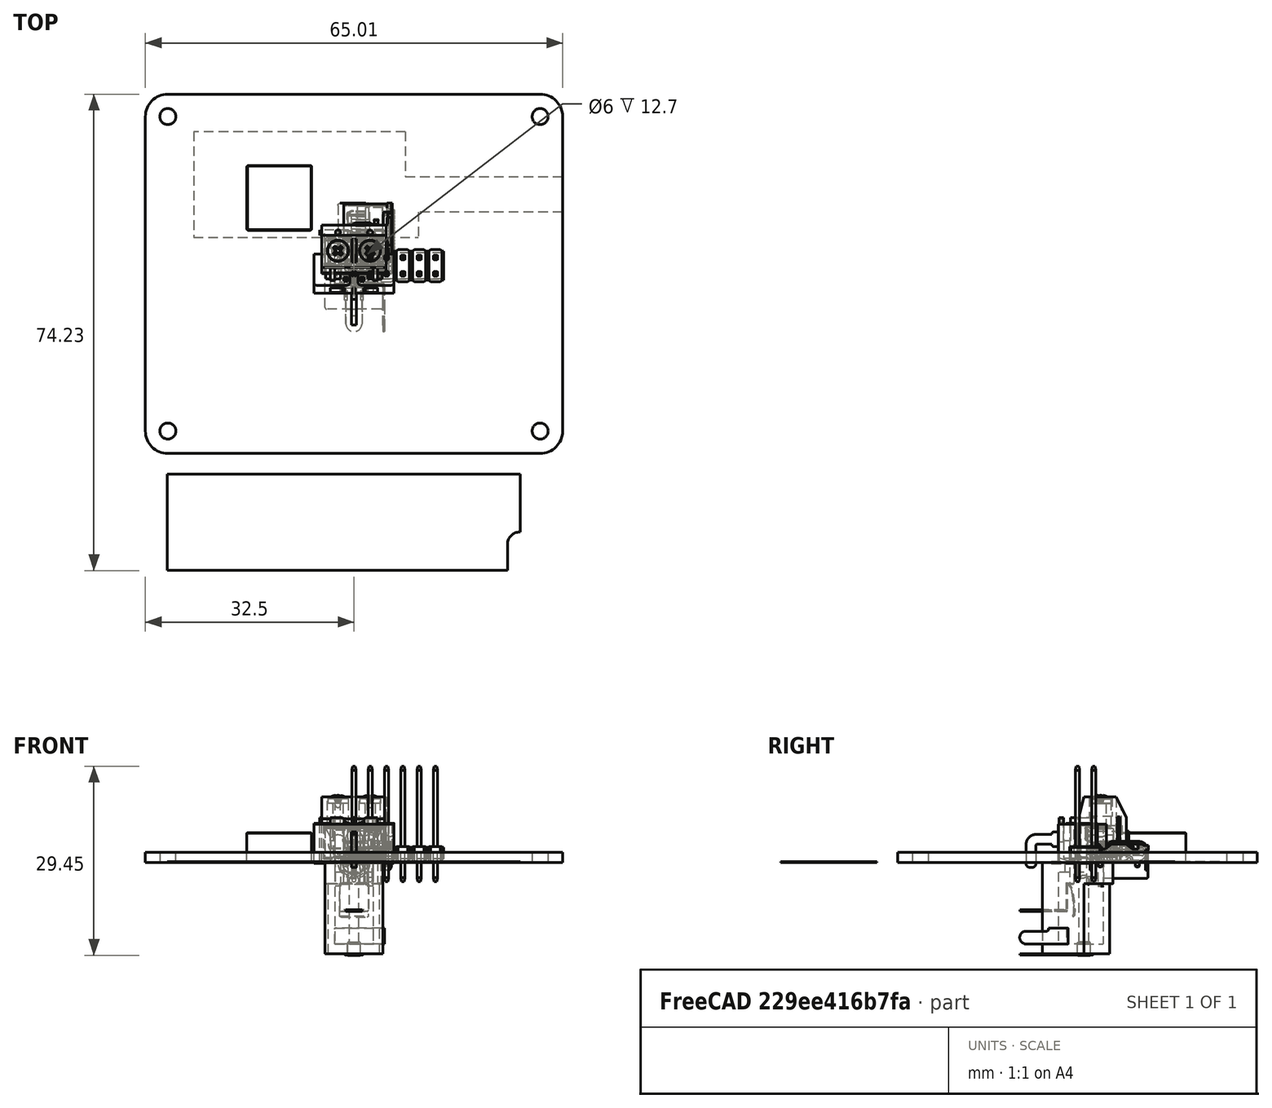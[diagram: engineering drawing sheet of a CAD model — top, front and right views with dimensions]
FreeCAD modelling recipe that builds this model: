
FCSTD DOCUMENT  (FreeCAD 1.0R39109 (Git))
Label: Yahboom PDB
License: All rights reserved
LicenseURL: https://en.wikipedia.org/wiki/All_rights_reserved
objects: Part::Feature×40, App::Link×16, App::FeaturePython×16, Sketcher::SketchObject×10, App::Part×9, PartDesign::Pad×7, PartDesign::Body×7, PartDesign::Fillet×5, App::DocumentObjectGroup×3, PartDesign::Pocket×2, PartDesign::Chamfer×2, Part::Extrusion×1, PartDesign::FeatureBase×1, Assembly::JointGroup×1, Assembly::AssemblyObject×1
note: 118 computed .brp shape members not serialized (recipe doc carries the construction recipe); baked Part::Feature solids carry a one-line shape summary decoded from their .brp

FEATURE [Sketcher::SketchObject] Sketch001
  ArcFitTolerance = 1e-06
  AttachmentSupport = -> [XY_Plane001]
  FullyConstrained = true
  MakeInternals = false
  MapMode = 5
  sketch-geometry (23):
    g0: LineSegment StartX=-32.5 StartY=24.5 StartZ=0 EndX=-32.5 EndY=-24.5 EndZ=0
    g1: LineSegment StartX=-29 StartY=-28 StartZ=0 EndX=29 EndY=-28 EndZ=0
    g2: LineSegment StartX=32.5 StartY=-24.5 StartZ=0 EndX=32.5 EndY=24.5 EndZ=0
    g3: LineSegment StartX=29 StartY=28 StartZ=0 EndX=-29 EndY=28 EndZ=0
    g4: Circle CenterX=-29 CenterY=-24.5 CenterZ=0 NormalX=0 NormalY=0 NormalZ=1 AngleXU=0 Radius=1.25
    g5: GeomPoint X=-32.5 Y=0 Z=0
    g6: GeomPoint X=0 Y=28 Z=0
    g7: Circle CenterX=29 CenterY=-24.5 CenterZ=0 NormalX=0 NormalY=0 NormalZ=1 AngleXU=0 Radius=1.25
    g8: LineSegment [constr] StartX=-29 StartY=-24.5 StartZ=0 EndX=29 EndY=-24.5 EndZ=0
    g9: LineSegment [constr] StartX=-29 StartY=-24.5 StartZ=0 EndX=-29 EndY=24.5 EndZ=0
    g10: LineSegment [constr] StartX=-29 StartY=24.5 StartZ=0 EndX=29 EndY=24.5 EndZ=0
    g11: Circle CenterX=-29 CenterY=24.5 CenterZ=0 NormalX=0 NormalY=0 NormalZ=1 AngleXU=0 Radius=1.25
    g12: Circle CenterX=29 CenterY=24.5 CenterZ=0 NormalX=0 NormalY=0 NormalZ=1 AngleXU=0 Radius=1.25
    g13: GeomPoint [constr] X=-29 Y=0 Z=0
    g14: ArcOfCircle CenterX=-29 CenterY=24.5 CenterZ=0 NormalX=0 NormalY=0 NormalZ=1 AngleXU=0 Radius=3.5 StartAngle=1.5708 EndAngle=3.14159
    g15: GeomPoint [constr] X=-32.5 Y=28 Z=0
    g16: ArcOfCircle CenterX=29 CenterY=24.5 CenterZ=0 NormalX=0 NormalY=0 NormalZ=1 AngleXU=0 Radius=3.5 StartAngle=0 EndAngle=1.5708
    g17: GeomPoint [constr] X=32.5 Y=28 Z=0
    g18: ArcOfCircle CenterX=-29 CenterY=-24.5 CenterZ=0 NormalX=0 NormalY=0 NormalZ=1 AngleXU=0 Radius=3.5 StartAngle=3.14159 EndAngle=4.71239
    g19: GeomPoint [constr] X=-32.5 Y=-28 Z=0
    g20: ArcOfCircle CenterX=29 CenterY=-24.5 CenterZ=0 NormalX=0 NormalY=0 NormalZ=1 AngleXU=0 Radius=3.5 StartAngle=4.71239 EndAngle=6.28319
    g21: GeomPoint [constr] X=32.5 Y=-28 Z=0
    g22: GeomPoint X=0 Y=24.5 Z=0
  constraints (50):
    c: Vertical(g0)
    c: Vertical(g2)
    c: Horizontal(g1)
    c: Horizontal(g3)
    c: DistanceX(g15,g17) = 65
    c: DistanceY(g19,g15) = 56
    c: Diameter(g4) = 2.5
    c: Symmetric(g15,g19,g5)
    c: Horizontal(g5,g-1)
    c: Symmetric(g17,g15,g6)
    c: Vertical(g6,g-1)
    c: Diameter(g7) = 2.5
    c: Horizontal(g4,g7)
    c: Coincident(g8,g4)
    c: Coincident(g8,g7)
    c: Vertical(g9)
    c: Coincident(g10,g9)
    c: Horizontal(g10)
    c: Coincident(g11,g9)
    c: Coincident(g12,g10)
    c: Diameter(g11) = 2.5
    c: Diameter(g12) = 2.5
    c: DistanceX(g8,g8) = 58
    c: DistanceY(g9,g9) = 49
    c: DistanceX(g10,g10) = 58
    c: Coincident(g9,g4)
    c: Symmetric(g9,g9,g13)
    c: Horizontal(g13,g-1)
    c: PointOnObject(g15,g0)
    c: PointOnObject(g15,g3)
    c: Tangent(g0,g14) = -1.5708
    c: Tangent(g3,g14) = -1.5708
    c: PointOnObject(g17,g2)
    c: PointOnObject(g17,g3)
    c: Tangent(g2,g16) = -1.5708
    c: Tangent(g3,g16) = -1.5708
    c: PointOnObject(g19,g0)
    c: PointOnObject(g19,g1)
    c: Tangent(g0,g18) = -1.5708
    c: Tangent(g1,g18) = -1.5708
    c: PointOnObject(g21,g1)
    c: PointOnObject(g21,g2)
    c: Tangent(g1,g20) = -1.5708
    c: Tangent(g2,g20) = -1.5708
    c: Radius(g14) = 3.5
    c: Radius(g16) = 3.5
    c: Radius(g20) = 3.5
    c: Radius(g18) = 3.5
    c: Symmetric(g10,g10,g22)
    c: Vertical(g22,g-1)
FEATURE [PartDesign::Pad] Pad
  Direction = (0,0,1)
  Length = 1.57
  Length2 = 10
  Profile = -> Sketch001
  ReferenceAxis = -> Sketch001 [N_Axis]
  Refine = true
  Suppressed = false
  Type = 0
FEATURE [PartDesign::Body] Body  label="Board"
  AllowCompound = false
  Group = -> [Sketch001,Pad]
  Origin = -> Origin001
  Tip = -> Pad
FEATURE [Part::Feature] Part__Feature001  label="XH 2,54_2p"
  shape: bbox 7.4 x 5.75 x 7 mm, 52 faces (baked)
FEATURE [Part::Feature] Part__Feature002  label="XH 2,54_2p001"
  shape: bbox 0.64 x 0.64 x 9.7 mm, 14 faces (baked)
FEATURE [Part::Feature] Part__Feature003  label="XH 2,54_2p002"
  shape: bbox 0.64 x 0.64 x 9.7 mm, 14 faces (baked)
FEATURE [App::Part] XH_2_54_2p  label="XH 2,54_2p003"
  Group = -> [Part__Feature001,Part__Feature002,Part__Feature003]
  Origin = -> Origin002
FEATURE [Part::Feature] Part__Feature005  label="DC_JACK v003"
  shape: bbox 3.248 x 11.62 x 12.45 mm, 13 faces (baked)
FEATURE [Part::Feature] Part__Feature006  label="DC_JACK v004"
  shape: bbox 4.51 x 8.656 x 5.34 mm, 18 faces (baked)
FEATURE [Part::Feature] Part__Feature007  label="DC_JACK v005"
  shape: bbox 7.75 x 7.5 x 2.5 mm, 13 faces (baked)
FEATURE [App::Link] DC_JACK_v006  label="DC_JACK v007"
  LinkPlacement = pos=(2.3,28,7.07) rot=(0,0.707107,0.707107;3.14159rad)
  LinkedObject = -> DC_JACK_v2
  Placement = pos=(2.3,28,7.07) rot=(0,0.707107,0.707107;3.14159rad)
FEATURE [App::Link] XH_2_54_2p003  label="XH 2,54_2p004"
  LinkPlacement = pos=(-8.13,21,4.445) rot=(1,0,0;4.71239rad)
  LinkedObject = -> XH_2_54_2p
  Placement = pos=(-8.13,21,4.445) rot=(1,0,0;4.71239rad)
FEATURE [Part::Feature] Part__Feature016  label="USB Type C"
  Placement = pos=(4.7601,6.43113,0.0823619) rot=(0.57735,0.57735,0.57735;2.0944rad)
  shape: bbox 7.401 x 8.941 x 4.471 mm, 192 faces (baked)
FEATURE [Part::Feature] Part__Feature017  label="USB Type C001"
  Placement = pos=(4.7601,6.43113,0.0823619) rot=(0.57735,0.57735,0.57735;2.0944rad)
  shape: bbox 0.5 x 0.3 x 1.1 mm, 6 faces (baked)
FEATURE [Part::Feature] Part__Feature018  label="USB Type C002"
  Placement = pos=(4.7601,6.43113,0.0823619) rot=(0.57735,0.57735,0.57735;2.0944rad)
  shape: bbox 7.5 x 9.2 x 3.55 mm, 355 faces (baked)
FEATURE [Part::Feature] Part__Feature019  label="USB Type C003"
  Placement = pos=(4.7601,6.43113,0.0823619) rot=(0.57735,0.57735,0.57735;2.0944rad)
  shape: bbox 0.5 x 0.3 x 1.1 mm, 6 faces (baked)
FEATURE [App::Part] USB_Type_C  label="USB Type C004"
  Group = -> [Part__Feature016,Part__Feature017,Part__Feature018,Part__Feature019]
  Origin = -> Origin007
FEATURE [Part::Feature] Part__Feature020  label="B2B-PH-K-S v3"
  shape: bbox 5.9 x 4.5 x 6 mm, 52 faces (baked)
FEATURE [Part::Feature] Part__Feature021  label="B2B-PH-K-S v004"
  shape: bbox 0.5 x 0.5 x 8.4 mm, 14 faces (baked)
FEATURE [Part::Feature] Part__Feature022  label="B2B-PH-K-S v005"
  shape: bbox 0.5 x 0.5 x 8.4 mm, 14 faces (baked)
FEATURE [App::Part] B2B_PH_K_S_v3  label="B2B-PH-K-S v006"
  Group = -> [Part__Feature020,Part__Feature021,Part__Feature022]
  Origin = -> Origin008
FEATURE [App::Link] DC_JACK_v007  label="DC_JACK v008"
  LinkPlacement = pos=(2.3,-28,7.07) rot=(1,0,0;1.5708rad)
  LinkedObject = -> DC_JACK_v2
  Placement = pos=(2.3,-28,7.07) rot=(1,0,0;1.5708rad)
FEATURE [App::Link] USB_Type_C004  label="USB Type C005"
  LinkPlacement = pos=(-15.0042,-27.4101,1.52835) rot=(0,0,1;1.5708rad)
  LinkedObject = -> USB_Type_C
  Placement = pos=(-15.0042,-27.4101,1.52835) rot=(0,0,1;1.5708rad)
FEATURE [App::Link] B2B_PH_K_S_v006  label="B2B-PH-K-S v007"
  LinkPlacement = pos=(-10,-22,6.07) rot=(0,0.707107,-0.707107;3.14159rad)
  LinkedObject = -> B2B_PH_K_S_v3
  Placement = pos=(-10,-22,6.07) rot=(0,0.707107,-0.707107;3.14159rad)
FEATURE [App::Link] B2B_PH_K_S_v007  label="B2B-PH-K-S v008"
  LinkPlacement = pos=(-3.6,-22,6.07) rot=(0,0.707107,-0.707107;3.14159rad)
  LinkedObject = -> B2B_PH_K_S_v3
  Placement = pos=(-3.6,-22,6.07) rot=(0,0.707107,-0.707107;3.14159rad)
FEATURE [Part::Feature] Part__Feature023  label="case"
  shape: bbox 10.35 x 7.6 x 10.2 mm, 52 faces (baked)
FEATURE [Part::Feature] Part__Feature024  label="Terminal1"
  Placement = pos=(2.5,5.6,0) rot=(0,0,1;0rad)
  shape: bbox 4 x 4.06 x 3.567 mm, 29 faces (baked)
FEATURE [Part::Feature] Part__Feature025  label="Terminal002"
  Placement = pos=(2.5,5.6,0) rot=(0,0,1;0rad)
  shape: bbox 4 x 4 x 9 mm, 10 faces (baked)
FEATURE [App::Part] Terminal1  label="Terminal003"
  Group = -> [Part__Feature024,Part__Feature025]
  Origin = -> Origin010
FEATURE [Part::Feature] Part__Feature026  label="Terminal004"
  Placement = pos=(-2.5,5.6,0) rot=(0,0,1;0rad)
  shape: bbox 4 x 4.06 x 3.567 mm, 29 faces (baked)
FEATURE [Part::Feature] Part__Feature027  label="Terminal005"
  Placement = pos=(-2.5,5.6,0) rot=(0,0,1;0rad)
  shape: bbox 4 x 4 x 9 mm, 10 faces (baked)
FEATURE [App::Part] Terminal002  label="Terminal006"
  Group = -> [Part__Feature026,Part__Feature027]
  Origin = -> Origin011
FEATURE [Part::Feature] Part__Feature028  label="Screw1"
  Placement = pos=(-2.5,3.6,9.2) rot=(0,0,1;0rad)
  shape: bbox 3.2 x 3.2 x 5.262 mm, 27 faces (baked)
FEATURE [Part::Feature] Part__Feature029  label="Screw002"
  Placement = pos=(2.5,3.6,9.2) rot=(0,0,1;0rad)
  shape: bbox 3.2 x 3.2 x 5.262 mm, 27 faces (baked)
FEATURE [App::Part] kf301_v1
  Group = -> [Part__Feature023,Terminal1,Terminal002,Part__Feature028,Part__Feature029]
  Origin = -> Origin009
FEATURE [App::Link] kf301_v002
  LinkPlacement = pos=(-19.5,27.6021,1.57) rot=(0,0,1;3.14159rad)
  LinkedObject = -> kf301_v1
  Placement = pos=(-19.5,27.6021,1.57) rot=(0,0,1;3.14159rad)
FEATURE [App::FeaturePython] Joint  label="Fixed"  # Assembly joint (typed FeaturePython)
  Activated = true
  AngleMax = 0
  AngleMin = 0
  Detach1 = false
  Detach2 = false
  Distance = 0
  Distance2 = 0
  EnableAngleMax = false
  EnableAngleMin = false
  EnableLengthMax = false
  EnableLengthMin = false
  JointType = 0 (Fixed)
  LengthMax = 0
  LengthMin = 0
  Offset1 = pos=(0,8,0) rot=(0,0,1;0rad)
  Placement1 = pos=(13,3.10207,2e-15) rot=(-0.57735,-0.57735,0.57735;4.18879rad)
  Placement2 = pos=(-32.5,24.5,1.57) rot=(-0.57735,-0.57735,0.57735;4.18879rad)
  Reference1 = -> Assembly [kf301_v002.Part__Feature023.Edge33,kf301_v002.Part__Feature023.Edge33]
  Reference2 = -> Assembly [Board.Edge4,Board.Vertex2]
FEATURE [App::FeaturePython] Joint001  label="Fixed001"  # Assembly joint (typed FeaturePython)
  Activated = true
  AngleMax = 0
  AngleMin = 0
  Detach1 = false
  Detach2 = false
  Distance = 0
  Distance2 = 0
  EnableAngleMax = false
  EnableAngleMin = false
  EnableLengthMax = false
  EnableLengthMin = false
  JointType = 0 (Fixed)
  LengthMax = 0
  LengthMin = 0
  Offset2 = pos=(0,20.67,-3.5) rot=(0,0,-1;1.5708rad)
  Placement1 = pos=(-3.7,2.875,7) rot=(0,1,0;3.14159rad)
  Placement2 = pos=(-11.83,28,1.57) rot=(0,-0.707107,0.707107;3.14159rad)
  Reference1 = -> Assembly [XH_2_54_2p003.Part__Feature001.Edge107,XH_2_54_2p003.Part__Feature001.Vertex73]
  Reference2 = -> Assembly [Board.Edge4,Board.Vertex2]
FEATURE [App::FeaturePython] Joint003  label="Fixed003"  # Assembly joint (typed FeaturePython)
  Activated = true
  AngleMax = 0
  AngleMin = 0
  Detach1 = false
  Detach2 = false
  Distance = 0
  Distance2 = 0
  EnableAngleMax = false
  EnableAngleMin = false
  EnableLengthMax = false
  EnableLengthMin = false
  JointType = 0 (Fixed)
  LengthMax = 0
  LengthMin = 0
  Offset2 = pos=(0,30.55,-3.6) rot=(0,0,-1;1.5708rad)
  Placement1 = pos=(-4.25,-5.5,-7.1) rot=(0,1,0;3.14159rad)
  Placement2 = pos=(-1.95,-20.9,1.57) rot=(0,-0.707107,0.707107;3.14159rad)
  Reference1 = -> Assembly [DC_JACK_v007.Part__Feature004.Edge68,DC_JACK_v007.Part__Feature004.Edge68]
  Reference2 = -> Assembly [Board.Edge4,Board.Vertex4]
FEATURE [Part::Feature] Part__Feature004  label="DC_JACK v2"
  shape: bbox 9 x 11 x 14.2 mm, 28 faces (baked)
FEATURE [App::Part] DC_JACK_v2  label="DC_JACK v006"
  Group = -> [Part__Feature004,Part__Feature005,Part__Feature006,Part__Feature007]
  Origin = -> Origin003
FEATURE [App::Link] Board  label="Board001"
  LinkedObject = -> Body
FEATURE [App::FeaturePython] GroundedJoint  # Assembly grounded joint (typed FeaturePython)
  ObjectToGround = -> Board
FEATURE [App::FeaturePython] Joint004  label="Fixed004"  # Assembly joint (typed FeaturePython)
  Activated = true
  AngleMax = 0
  AngleMin = 0
  Detach1 = false
  Detach2 = false
  Distance = 0
  Distance2 = 0
  EnableAngleMax = false
  EnableAngleMin = false
  EnableLengthMax = false
  EnableLengthMin = false
  JointType = 0 (Fixed)
  LengthMax = 0
  LengthMin = 0
  Offset2 = pos=(0,30.55,-3.5) rot=(0,0,1;1.5708rad)
  Placement1 = pos=(4.25,-5.5,0) rot=(0,1,0;3.14159rad)
  Placement2 = pos=(-1.95,28,1.57) rot=(-1,0,0;4.71239rad)
  Reference1 = -> Assembly [DC_JACK_v006.Part__Feature004.Edge70,DC_JACK_v006.Part__Feature004.Vertex46]
  Reference2 = -> Assembly [Board.Edge4,Board.Vertex2]
FEATURE [App::FeaturePython] Joint005  label="Fixed005"  # Assembly joint (typed FeaturePython)
  Activated = true
  AngleMax = 0
  AngleMin = 0
  Detach1 = false
  Detach2 = false
  Distance = 0
  Distance2 = 0
  EnableAngleMax = false
  EnableAngleMin = false
  EnableLengthMax = false
  EnableLengthMin = false
  JointType = 0 (Fixed)
  LengthMax = 0
  LengthMin = 0
  Offset2 = pos=(0,1,5.85) rot=(0,0,-1;1.5708rad)
  Placement1 = pos=(1.71465,-0.0407081,-6.35) rot=(0.707107,0,0.707107;3.14159rad)
  Placement2 = pos=(-23.15,-29,1.57) rot=(0.57735,0.57735,0.57735;2.0944rad)
  Reference1 = -> Assembly [USB_Type_C004.Part__Feature016.Edge38,USB_Type_C004.Part__Feature016.Edge38]
  Reference2 = -> Assembly [Board.Edge10,Board.Vertex6]
FEATURE [App::FeaturePython] Joint006  label="Fixed006"  # Assembly joint (typed FeaturePython)
  Activated = true
  AngleMax = 0
  AngleMin = 0
  Detach1 = false
  Detach2 = false
  Distance = 0
  Distance2 = 0
  EnableAngleMax = false
  EnableAngleMin = false
  EnableLengthMax = false
  EnableLengthMin = false
  JointType = 0 (Fixed)
  LengthMax = 0
  LengthMin = 0
  Offset2 = pos=(0,16.6,0.5) rot=(0,0,1;1.5708rad)
  Placement1 = pos=(5.9,4.5,3) rot=(0,1,0;3.14159rad)
  Placement2 = pos=(-15.9,-25,1.57) rot=(-1,0,0;4.71239rad)
  Reference1 = -> Assembly [B2B_PH_K_S_v006.Part__Feature020.Edge155,B2B_PH_K_S_v006.Part__Feature020.Edge155]
  Reference2 = -> Assembly [Board.Edge4,Board.Vertex4]
FEATURE [App::FeaturePython] Joint007  label="Fixed007"  # Assembly joint (typed FeaturePython)
  Activated = true
  AngleMax = 0
  AngleMin = 0
  Detach1 = false
  Detach2 = false
  Distance = 0
  Distance2 = 0
  EnableAngleMax = false
  EnableAngleMin = false
  EnableLengthMax = false
  EnableLengthMin = false
  JointType = 0 (Fixed)
  LengthMax = 0
  LengthMin = 0
  Offset2 = pos=(0,23,0.5) rot=(0,0,1;1.5708rad)
  Placement1 = pos=(5.9,4.5,3) rot=(0,1,0;3.14159rad)
  Placement2 = pos=(-9.5,-25,1.57) rot=(-1,0,0;4.71239rad)
  Reference1 = -> Assembly [B2B_PH_K_S_v007.Part__Feature020.Edge155,B2B_PH_K_S_v007.Part__Feature020.Edge155]
  Reference2 = -> Assembly [Board.Edge4,Board.Vertex4]
FEATURE [Part::Feature] Part__Feature  label="4.7uF 63V electr 5 x11mm -P.diameter 2.5mm-Green-Yellow"
  shape: bbox 5.721 x 15.1 x 5.727 mm, 151 faces (baked)
FEATURE [App::Link] __7uF_63V_electr_5_x11mm__P_diameter_2_5mm_Green_Yellow  label="4.7uF 63V electr 5 x11mm -P.diameter 2.5mm-Green-Yellow001"
  LinkPlacement = pos=(29.0455,3.315,4.13) rot=(0,0,1;0rad)
  LinkedObject = -> Part__Feature
  Placement = pos=(29.0455,3.315,4.13) rot=(0,0,1;0rad)
FEATURE [App::Link] __7uF_63V_electr_5_x11mm__P_diameter_2_5mm_Green_Yellow001  label="4.7uF 63V electr 5 x11mm -P.diameter 2.5mm-Green-Yellow002"
  LinkPlacement = pos=(-29.0458,3.3,4.145) rot=(0,0,1;0rad)
  LinkedObject = -> Part__Feature
  Placement = pos=(-29.0458,3.3,4.145) rot=(0,0,1;0rad)
FEATURE [App::Link] __7uF_63V_electr_5_x11mm__P_diameter_2_5mm_Green_Yellow002  label="4.7uF 63V electr 5 x11mm -P.diameter 2.5mm-Green-Yellow003"
  LinkPlacement = pos=(-29.0458,-3.65,4.145) rot=(0,0,1;3.14159rad)
  LinkedObject = -> Part__Feature
  Placement = pos=(-29.0458,-3.65,4.145) rot=(0,0,1;3.14159rad)
FEATURE [App::FeaturePython] Joint008  label="Fixed008"  # Assembly joint (typed FeaturePython)
  Activated = true
  AngleMax = 0
  AngleMin = 0
  Detach1 = false
  Detach2 = false
  Distance = 0
  Distance2 = 0
  EnableAngleMax = false
  EnableAngleMin = false
  EnableLengthMax = false
  EnableLengthMin = false
  JointType = 0 (Fixed)
  LengthMax = 0
  LengthMin = 0
  Offset2 = pos=(-2.5,13.75,-1) rot=(0,0,1;3.14159rad)
  Placement1 = pos=(0.9545,10.935,-0.06) rot=(0.707107,0,0.707107;3.14159rad)
  Placement2 = pos=(30,14.25,4.07) rot=(0,1,0;4.71239rad)
  Reference1 = -> Assembly [__7uF_63V_electr_5_x11mm__P_diameter_2_5mm_Green_Yellow.Edge464,__7uF_63V_electr_5_x11mm__P_diameter_2_5mm_Green_Yellow.Edge464]
  Reference2 = -> Assembly [Board.Edge22,Board.Vertex14]
FEATURE [App::FeaturePython] Joint009  label="Fixed009"  # Assembly joint (typed FeaturePython)
  Activated = true
  AngleMax = 0
  AngleMin = 0
  Detach1 = false
  Detach2 = false
  Distance = 0
  Distance2 = 0
  EnableAngleMax = false
  EnableAngleMin = false
  EnableLengthMax = false
  EnableLengthMin = false
  JointType = 0 (Fixed)
  LengthMax = 0
  LengthMin = 0
  Offset2 = pos=(-2.5,13.75,1) rot=(0,0,1;0rad)
  Placement1 = pos=(-0.954218,10.95,-0.075) rot=(-0.707107,0,0.707107;3.14159rad)
  Placement2 = pos=(-30,14.25,4.07) rot=(-0.707107,0,0.707107;3.14159rad)
  Reference1 = -> Assembly [__7uF_63V_electr_5_x11mm__P_diameter_2_5mm_Green_Yellow001.Edge490,__7uF_63V_electr_5_x11mm__P_diameter_2_5mm_Green_Yellow001.Edge490]
  Reference2 = -> Assembly [Board.Edge22,Board.Vertex16]
FEATURE [App::FeaturePython] Joint010  label="Fixed010"  # Assembly joint (typed FeaturePython)
  Activated = true
  AngleMax = 0
  AngleMin = 0
  Detach1 = false
  Detach2 = false
  Distance = 0
  Distance2 = 0
  EnableAngleMax = false
  EnableAngleMin = false
  EnableLengthMax = false
  EnableLengthMin = false
  JointType = 0 (Fixed)
  LengthMax = 0
  LengthMin = 0
  Offset2 = pos=(2.5,-13.4,-1) rot=(0,0,1;3.14159rad)
  Placement1 = pos=(0.954218,10.95,-0.075) rot=(-0.707107,0,0.707107;3.14159rad)
  Placement2 = pos=(-30,-14.6,4.07) rot=(0,-1,0;4.71239rad)
  Reference1 = -> Assembly [__7uF_63V_electr_5_x11mm__P_diameter_2_5mm_Green_Yellow002.Edge463,__7uF_63V_electr_5_x11mm__P_diameter_2_5mm_Green_Yellow002.Edge463]
  Reference2 = -> Assembly [Board.Edge10,Board.Vertex6]
FEATURE [Part::Feature] Part__Feature030  label="DS1021_black_2x06p_100mil_Type5_rev1.0"
  shape: bbox 0.64 x 0.64 x 18 mm, 18 faces (baked)
FEATURE [Part::Feature] Part__Feature031  label="DS1021_black_2x06p_100mil_Type5_rev1.001"
  shape: bbox 2.54 x 5 x 2.5 mm, 30 faces (baked)
FEATURE [Part::Feature] Part__Feature032  label="DS1021_black_2x06p_100mil_Type5_rev1.002"
  shape: bbox 2.54 x 5 x 2.5 mm, 30 faces (baked)
FEATURE [Part::Feature] Part__Feature033  label="DS1021_black_2x06p_100mil_Type5_rev1.003"
  shape: bbox 0.64 x 0.64 x 18 mm, 18 faces (baked)
FEATURE [Part::Feature] Part__Feature034  label="DS1021_black_2x06p_100mil_Type5_rev1.004"
  shape: bbox 0.64 x 0.64 x 18 mm, 18 faces (baked)
FEATURE [Part::Feature] Part__Feature035  label="DS1021_black_2x06p_100mil_Type5_rev1.005"
  shape: bbox 0.64 x 0.64 x 18 mm, 18 faces (baked)
FEATURE [Part::Feature] Part__Feature036  label="DS1021_black_2x06p_100mil_Type5_rev1.006"
  shape: bbox 0.64 x 0.64 x 18 mm, 18 faces (baked)
FEATURE [Part::Feature] Part__Feature037  label="DS1021_black_2x06p_100mil_Type5_rev1.007"
  shape: bbox 0.64 x 0.64 x 18 mm, 18 faces (baked)
FEATURE [Part::Feature] Part__Feature008  label="DS1021_black_2x06p_100mil_Type5_rev1.008"
  shape: bbox 2.54 x 5 x 2.5 mm, 30 faces (baked)
FEATURE [Part::Feature] Part__Feature009  label="DS1021_black_2x06p_100mil_Type5_rev1.009"
  shape: bbox 0.64 x 0.64 x 18 mm, 18 faces (baked)
FEATURE [Part::Feature] Part__Feature010  label="DS1021_black_2x06p_100mil_Type5_rev1.010"
  shape: bbox 0.64 x 0.64 x 18 mm, 18 faces (baked)
FEATURE [Part::Feature] Part__Feature011  label="DS1021_black_2x06p_100mil_Type5_rev1.011"
  shape: bbox 2.54 x 5 x 2.5 mm, 30 faces (baked)
FEATURE [Part::Feature] Part__Feature012  label="DS1021_black_2x06p_100mil_Type5_rev1.012"
  shape: bbox 2.54 x 5 x 2.5 mm, 30 faces (baked)
FEATURE [Part::Feature] Part__Feature013  label="DS1021_black_2x06p_100mil_Type5_rev1.013"
  shape: bbox 0.64 x 0.64 x 18 mm, 18 faces (baked)
FEATURE [Part::Feature] Part__Feature014  label="DS1021_black_2x06p_100mil_Type5_rev1.014"
  shape: bbox 0.64 x 0.64 x 18 mm, 18 faces (baked)
FEATURE [Part::Feature] Part__Feature015  label="DS1021_black_2x06p_100mil_Type5_rev1.015"
  shape: bbox 0.64 x 0.64 x 18 mm, 18 faces (baked)
FEATURE [Part::Feature] Part__Feature038  label="DS1021_black_2x06p_100mil_Type5_rev1.016"
  shape: bbox 0.64 x 0.64 x 18 mm, 18 faces (baked)
FEATURE [Part::Feature] Part__Feature039  label="DS1021_black_2x06p_100mil_Type5_rev1.017"
  shape: bbox 2.54 x 5 x 2.5 mm, 60 faces (baked)
FEATURE [App::Part] DS1021_black_2x06p_100mil_Type5_rev1_0  label="DS1021_black_2x06p_100mil_Type5_rev1.018"
  Group = -> [Part__Feature030,Part__Feature031,Part__Feature032,Part__Feature033,Part__Feature034,Part__Feature035,Part__Feature036,Part__Feature037,Part__Feature008,Part__Feature009,Part__Feature010,Part__Feature011,Part__Feature012,Part__Feature013,Part__Feature014,Part__Feature015,Part__Feature038,Part__Feature039]
  Origin = -> Origin012
FEATURE [App::Link] DS1021_black_2x06p_100mil_Type5_rev1_018  label="DS1021_black_2x06p_100mil_Type5_rev1.019"
  LinkPlacement = pos=(10.43,-13.025,2.77) rot=(1,0,0;1.5708rad)
  LinkedObject = -> DS1021_black_2x06p_100mil_Type5_rev1_0
  Placement = pos=(10.43,-13.025,2.77) rot=(1,0,0;1.5708rad)
FEATURE [App::FeaturePython] Joint011  label="Fixed011"  # Assembly joint (typed FeaturePython)
  Activated = true
  AngleMax = 0
  AngleMin = 0
  Detach1 = false
  Detach2 = false
  Distance = 0
  Distance2 = 0
  EnableAngleMax = false
  EnableAngleMin = false
  EnableLengthMax = false
  EnableLengthMin = false
  JointType = 0 (Fixed)
  LengthMax = 0
  LengthMin = 0
  Offset2 = pos=(0.2,-8.1,10) rot=(0,0,-1;1.5708rad)
  Placement1 = pos=(13.97,-1,1.475) rot=(0,1,0;3.14159rad)
  Placement2 = pos=(24.4,-14.5,1.77) rot=(0,0.707107,0.707107;3.14159rad)
  Reference1 = -> Assembly [DS1021_black_2x06p_100mil_Type5_rev1_018.Part__Feature012.Edge33,DS1021_black_2x06p_100mil_Type5_rev1_018.Part__Feature012.Edge33]
  Reference2 = -> Assembly [Board.Edge16,Board.Vertex10]
FEATURE [Sketcher::SketchObject] Sketch
  ArcFitTolerance = 1e-06
  FullyConstrained = true
  MakeInternals = false
  MapMode = 5
  sketch-geometry (6):
    g0: LineSegment StartX=6.25 StartY=-3 StartZ=0 EndX=6.25 EndY=3 EndZ=0
    g1: LineSegment StartX=6.25 StartY=3 StartZ=0 EndX=-6.25 EndY=3 EndZ=0
    g2: LineSegment StartX=-6.25 StartY=3 StartZ=0 EndX=-6.25 EndY=-3 EndZ=0
    g3: LineSegment StartX=-6.25 StartY=-3 StartZ=0 EndX=6.25 EndY=-3 EndZ=0
    g4: GeomPoint X=-6.25 Y=0 Z=0
    g5: GeomPoint X=0 Y=3 Z=0
  constraints (14):
    c: Coincident(g0,g1)
    c: Coincident(g1,g2)
    c: Coincident(g2,g3)
    c: Coincident(g3,g0)
    c: Vertical(g0)
    c: Vertical(g2)
    c: Horizontal(g1)
    c: Horizontal(g3)
    c: DistanceX(g1,g1) = 12.5
    c: DistanceY(g2,g2) = 6
    c: Symmetric(g2,g2,g4)
    c: Symmetric(g1,g1,g5)
    c: Vertical(g5,g-1)
    c: Horizontal(g4,g-1)
FEATURE [PartDesign::Pad] Pad001
  Direction = (0,0,1)
  Length = 6
  Length2 = 10
  Profile = -> Sketch
  ReferenceAxis = -> Sketch [N_Axis]
  Refine = true
  Suppressed = false
  Type = 0
FEATURE [Sketcher::SketchObject] Sketch002
  ArcFitTolerance = 1e-06
  AttachmentSupport = -> [YZ_Plane014]
  ExternalGeometry = -> [Pad001]
  FullyConstrained = true
  MakeInternals = false
  MapMode = 5
  Placement = pos=(0,0,0) rot=(0.57735,0.57735,0.57735;2.0944rad)
  sketch-geometry (12):
    g0: LineSegment StartX=-1.8 StartY=6 StartZ=0 EndX=3.1 EndY=6 EndZ=0
    g1: LineSegment StartX=3.1 StartY=6 StartZ=0 EndX=3.1 EndY=6.1 EndZ=0
    g2: LineSegment StartX=3.1 StartY=6.1 StartZ=0 EndX=-1.8 EndY=6.1 EndZ=0
    g3: LineSegment StartX=-1.8 StartY=6.1 StartZ=0 EndX=-1.8 EndY=6 EndZ=0
    g4: LineSegment StartX=3.1 StartY=6 StartZ=0 EndX=3 EndY=6 EndZ=0
    g5: LineSegment StartX=3 StartY=6 StartZ=0 EndX=3 EndY=-0.1 EndZ=0
    g6: LineSegment StartX=3 StartY=-0.1 StartZ=0 EndX=3.1 EndY=-0.1 EndZ=0
    g7: LineSegment StartX=3.1 StartY=-0.1 StartZ=0 EndX=3.1 EndY=6 EndZ=0
    g8: LineSegment StartX=3 StartY=-0.1 StartZ=0 EndX=3 EndY=-1e-16 EndZ=0
    g9: LineSegment StartX=3 StartY=-1e-16 StartZ=0 EndX=-1.8 EndY=-1e-16 EndZ=0
    g10: LineSegment StartX=-1.8 StartY=-1e-16 StartZ=0 EndX=-1.8 EndY=-0.1 EndZ=0
    g11: LineSegment StartX=-1.8 StartY=-0.1 StartZ=0 EndX=3 EndY=-0.1 EndZ=0
  constraints (34):
    c: Coincident(g0,g1)
    c: Coincident(g1,g2)
    c: Coincident(g2,g3)
    c: Coincident(g3,g0)
    c: Horizontal(g0)
    c: Horizontal(g2)
    c: Vertical(g1)
    c: Vertical(g3)
    c: Coincident(g4,g5)
    c: Coincident(g5,g6)
    c: Coincident(g6,g7)
    c: Coincident(g7,g4)
    c: Horizontal(g4)
    c: Horizontal(g6)
    c: Vertical(g5)
    c: Vertical(g7)
    c: Coincident(g4,g0)
    c: Coincident(g8,g9)
    c: Coincident(g9,g10)
    c: Coincident(g10,g11)
    c: Coincident(g11,g8)
    c: Vertical(g8)
    c: Vertical(g10)
    c: Horizontal(g9)
    c: Horizontal(g11)
    c: Coincident(g8,g5)
    c: Distance(g11,g9) = 0.1
    c: Distance(g7,g5) = 0.1
    c: Distance(g0,g2) = 0.1
    c: Distance(g-3,g3) = 1.2
    c: Vertical(g0,g9)
    c: Distance(g9,g0) = 6
    c: Distance(g-1,g0) = 6
    c: Distance(g-1,g5) = 3
FEATURE [Part::Extrusion] Extrude
  Base = -> Sketch002
  Dir = (1,0,0)
  DirMode = 2
  FaceMakerClass = Part::FaceMakerBullseye
  FaceMakerMode = 3
  LengthFwd = 12.5
  LengthRev = 0
  Solid = true
  Symmetric = true
FEATURE [Sketcher::SketchObject] Sketch003
  ArcFitTolerance = 1e-06
  AttachmentSupport = -> [Extrude]
  ExternalGeometry = -> [Extrude]
  FullyConstrained = true
  MakeInternals = false
  MapMode = 5
  Placement = pos=(0,0,6.1) rot=(0,0,1;0rad)
  sketch-geometry (14):
    g0: LineSegment StartX=-0.625 StartY=-1.8 StartZ=0 EndX=0.625 EndY=-1.8 EndZ=0
    g1: LineSegment StartX=0.625 StartY=-1.8 StartZ=0 EndX=0.625 EndY=0.7 EndZ=0
    g2: LineSegment StartX=0.625 StartY=0.7 StartZ=0 EndX=-0.625 EndY=0.7 EndZ=0
    g3: LineSegment StartX=-0.625 StartY=0.7 StartZ=0 EndX=-0.625 EndY=-1.8 EndZ=0
    g4: GeomPoint X=-2e-16 Y=-1.8 Z=0
    g5: GeomPoint X=-2e-16 Y=-1.8 Z=0
    g6: LineSegment StartX=2.125 StartY=0.7 StartZ=0 EndX=2.125 EndY=-0.8 EndZ=0
    g7: LineSegment StartX=2.125 StartY=-0.8 StartZ=0 EndX=4.375 EndY=-0.8 EndZ=0
    g8: LineSegment StartX=4.375 StartY=-0.8 StartZ=0 EndX=4.375 EndY=0.7 EndZ=0
    g9: LineSegment StartX=4.375 StartY=0.7 StartZ=0 EndX=2.125 EndY=0.7 EndZ=0
    g10: LineSegment StartX=-2.125 StartY=0.7 StartZ=0 EndX=-4.375 EndY=0.7 EndZ=0
    g11: LineSegment StartX=-4.375 StartY=0.7 StartZ=0 EndX=-4.375 EndY=-0.8 EndZ=0
    g12: LineSegment StartX=-4.375 StartY=-0.8 StartZ=0 EndX=-2.125 EndY=-0.8 EndZ=0
    g13: LineSegment StartX=-2.125 StartY=-0.8 StartZ=0 EndX=-2.125 EndY=0.7 EndZ=0
  constraints (38):
    c: Coincident(g0,g1)
    c: Coincident(g1,g2)
    c: Coincident(g2,g3)
    c: Coincident(g3,g0)
    c: Horizontal(g0)
    c: Horizontal(g2)
    c: Vertical(g1)
    c: Vertical(g3)
    c: Symmetric(g-3,g-3,g4)
    c: Symmetric(g0,g0,g5)
    c: Vertical(g4,g5)
    c: DistanceX(g2,g2) = 1.25
    c: DistanceY(g1,g1) = 2.5
    c: Coincident(g6,g7)
    c: Coincident(g7,g8)
    c: Coincident(g8,g9)
    c: Coincident(g9,g6)
    c: Vertical(g6)
    c: Vertical(g8)
    c: Horizontal(g7)
    c: Horizontal(g9)
    c: DistanceX(g9,g9) = 2.25
    c: DistanceY(g6,g6) = 1.5
    c: Distance(g1,g6) = 1.5
    c: Horizontal(g1,g6)
    c: Distance(g-3,g7) = 1
    c: Coincident(g10,g11)
    c: Coincident(g11,g12)
    c: Coincident(g12,g13)
    c: Coincident(g13,g10)
    c: Horizontal(g10)
    c: Horizontal(g12)
    c: Vertical(g11)
    c: Vertical(g13)
    c: Horizontal(g10,g2)
    c: DistanceX(g10,g10) = 2.25
    c: DistanceY(g13,g13) = 1.5
    c: Distance(g3,g13) = 1.5
FEATURE [PartDesign::FeatureBase] BaseFeature
  BaseFeature = -> Extrude
  Suppressed = false
FEATURE [PartDesign::Pocket] Pocket
  BaseFeature = -> BaseFeature
  Direction = (0,0,-1)
  Length = 5
  Length2 = 5
  Profile = -> Sketch003
  ReferenceAxis = -> Sketch003 [N_Axis]
  Refine = true
  Suppressed = false
  Type = 0
FEATURE [PartDesign::Fillet] Fillet
  Base = -> Pocket [Edge32,Edge35,Edge39,Edge37,Edge31,Edge23,Edge19,Edge27]
  BaseFeature = -> Pocket
  Radius = 0.5
  Refine = true
  SupportTransform = false
  Suppressed = false
  UseAllEdges = false
FEATURE [App::DocumentObjectGroup] Group002  label="Group"
FEATURE [Sketcher::SketchObject] Sketch005
  ArcFitTolerance = 1e-06
  AttachmentSupport = -> [Fillet]
  FullyConstrained = true
  MakeInternals = false
  MapMode = 5
  Placement = pos=(0,3,0) rot=(1,0,0;1.5708rad)
  sketch-geometry (5):
    g0: LineSegment StartX=-3.25 StartY=5 StartZ=0 EndX=-3.25 EndY=1 EndZ=0
    g1: LineSegment StartX=-3.25 StartY=1 StartZ=0 EndX=3.25 EndY=1 EndZ=0
    g2: LineSegment StartX=3.25 StartY=1 StartZ=0 EndX=3.25 EndY=5 EndZ=0
    g3: LineSegment StartX=3.25 StartY=5 StartZ=0 EndX=-3.25 EndY=5 EndZ=0
    g4: GeomPoint X=0 Y=1 Z=0
  constraints (13):
    c: Coincident(g0,g1)
    c: Coincident(g1,g2)
    c: Coincident(g2,g3)
    c: Coincident(g3,g0)
    c: Vertical(g0)
    c: Vertical(g2)
    c: Horizontal(g1)
    c: Horizontal(g3)
    c: DistanceY(g2,g2) = 4
    c: DistanceX(g3,g3) = 6.5
    c: Symmetric(g1,g1,g4)
    c: Vertical(g-1,g4)
    c: Distance(g1,g-1) = 1
FEATURE [PartDesign::Pocket] Pocket001
  BaseFeature = -> Fillet
  Direction = (0,1,-2e-16)
  Length = 5
  Length2 = 5
  Profile = -> Sketch005
  ReferenceAxis = -> Sketch005 [N_Axis]
  Refine = true
  Suppressed = false
  Type = 0
FEATURE [PartDesign::Body] Body001  label="Casing"
  AllowCompound = false
  BaseFeature = -> Extrude
  Group = -> [BaseFeature,Sketch003,Pocket,Fillet,Sketch005,Pocket001]
  Origin = -> Origin015
  Tip = -> Pocket001
FEATURE [Sketcher::SketchObject] Sketch006
  ArcFitTolerance = 1e-06
  AttachmentSupport = -> [XZ_Plane016]
  FullyConstrained = true
  MakeInternals = false
  MapMode = 5
  Placement = pos=(0,0,0) rot=(1,0,0;1.5708rad)
  sketch-geometry (4):
    g0: LineSegment StartX=3.25 StartY=4.9 StartZ=0 EndX=-0.55 EndY=4.9 EndZ=0
    g1: LineSegment StartX=-0.55 StartY=4.9 StartZ=0 EndX=-0.55 EndY=1.1 EndZ=0
    g2: LineSegment StartX=-0.55 StartY=1.1 StartZ=0 EndX=3.25 EndY=1.1 EndZ=0
    g3: LineSegment StartX=3.25 StartY=1.1 StartZ=0 EndX=3.25 EndY=4.9 EndZ=0
  constraints (12):
    c: Coincident(g0,g1)
    c: Coincident(g1,g2)
    c: Coincident(g2,g3)
    c: Coincident(g3,g0)
    c: Horizontal(g0)
    c: Horizontal(g2)
    c: Vertical(g1)
    c: Vertical(g3)
    c: DistanceX(g0,g0) = 3.8
    c: DistanceY(g1,g1) = 3.8
    c: Distance(g-1,g2) = 1.1
    c: Distance(g-2,g3) = 3.25
FEATURE [PartDesign::Pad] Pad002
  BaseFeature = -> Pad001
  Direction = (0,-1,2e-16)
  Length = 8
  Length2 = 10
  Profile = -> Sketch006
  ReferenceAxis = -> Sketch006 [N_Axis]
  Refine = true
  Reversed = true
  Suppressed = false
  Type = 0
FEATURE [PartDesign::Chamfer] Chamfer
  Angle = 60
  Base = -> Pad002 [Edge24,Edge21]
  BaseFeature = -> Pad002
  ChamferType = 2
  FlipDirection = false
  Refine = true
  Size = 0.5
  Size2 = 1
  SupportTransform = false
  Suppressed = false
  UseAllEdges = false
FEATURE [PartDesign::Body] Body002  label="Body + Knob"
  AllowCompound = false
  Group = -> [Pad001,Sketch,Sketch006,Pad002,Chamfer]
  Origin = -> Origin016
  Tip = -> Chamfer
FEATURE [Sketcher::SketchObject] Sketch007
  ArcFitTolerance = 1e-06
  AttachmentSupport = -> [YZ_Plane017]
  FullyConstrained = true
  MakeInternals = false
  MapMode = 5
  Placement = pos=(0,0,0) rot=(0.57735,0.57735,0.57735;2.0944rad)
  sketch-geometry (10):
    g0: LineSegment StartX=-3 StartY=4.75 StartZ=0 EndX=-4 EndY=4.75 EndZ=0
    g1: LineSegment StartX=-4 StartY=2.5 StartZ=0 EndX=-3 EndY=2.5 EndZ=0
    g2: LineSegment StartX=-3 StartY=4.75 StartZ=0 EndX=-3 EndY=2.5 EndZ=0
    g3: LineSegment StartX=-4 StartY=4.375 StartZ=0 EndX=-8 EndY=4.375 EndZ=0
    g4: LineSegment StartX=-8 StartY=4.375 StartZ=0 EndX=-8 EndY=-0.75 EndZ=0
    g5: LineSegment StartX=-4 StartY=2.875 StartZ=0 EndX=-6.5 EndY=2.875 EndZ=0
    g6: LineSegment StartX=-6.5 StartY=2.875 StartZ=0 EndX=-6.5 EndY=-0.75 EndZ=0
    g7: LineSegment StartX=-4 StartY=4.75 StartZ=0 EndX=-4 EndY=4.375 EndZ=0
    g8: LineSegment StartX=-4 StartY=2.875 StartZ=0 EndX=-4 EndY=2.5 EndZ=0
    g9: LineSegment StartX=-8 StartY=-0.75 StartZ=0 EndX=-6.5 EndY=-0.75 EndZ=0
  constraints (30):
    c: Horizontal(g0)
    c: Horizontal(g1)
    c: DistanceX(g0,g0) = 1
    c: Distance(g1,g0) = 2.25
    c: Coincident(g2,g0)
    c: Vertical(g2)
    c: Coincident(g1,g2)
    c: Distance(g-2,g2) = 3
    c: Horizontal(g3)
    c: Coincident(g4,g3)
    c: Vertical(g4)
    c: Horizontal(g5)
    c: Coincident(g6,g5)
    c: Vertical(g6)
    c: Distance(g5,g3) = 1.5
    c: Distance(g6,g4) = 1.5
    c: Distance(g-1,g5) = 2.875
    c: Distance(g-1,g1) = 2.5
    c: DistanceX(g3,g3) = 4
    c: Coincident(g7,g3)
    c: Vertical(g7)
    c: Coincident(g8,g5)
    c: Coincident(g8,g1)
    c: Vertical(g8)
    c: Coincident(g0,g7)
    c: Vertical(g5,g3)
    c: Coincident(g9,g4)
    c: Coincident(g9,g6)
    c: Horizontal(g9)
    c: DistanceY(g6,g6) = 3.625
FEATURE [PartDesign::Pad] Pad003
  Direction = (1,0,0)
  Length = 0.75
  Length2 = 10
  Midplane = true
  Placement = pos=(0,0,0) rot=(1,1,1;2.0944rad)
  Profile = -> Sketch007
  ReferenceAxis = -> Sketch007 [N_Axis]
  Refine = true
  Suppressed = false
  Type = 0
FEATURE [PartDesign::Fillet] Fillet001
  Base = -> Pad003 [Edge17]
  BaseFeature = -> Pad003
  Placement = pos=(0,0,0) rot=(1,1,1;2.0944rad)
  Radius = 1.5
  Refine = true
  SupportTransform = false
  Suppressed = false
  UseAllEdges = false
FEATURE [PartDesign::Fillet] Fillet002
  Base = -> Fillet001 [Edge17,Edge32,Edge31]
  BaseFeature = -> Fillet001
  Placement = pos=(0,0,0) rot=(1,1,1;2.0944rad)
  Radius = 0.25
  Refine = true
  SupportTransform = false
  Suppressed = false
  UseAllEdges = false
FEATURE [PartDesign::Fillet] Fillet003
  Base = -> Fillet002 [Edge28,Edge32]
  BaseFeature = -> Fillet002
  Placement = pos=(0,0,0) rot=(1,1,1;2.0944rad)
  Radius = 0.5
  Refine = true
  SupportTransform = false
  Suppressed = false
  UseAllEdges = false
FEATURE [PartDesign::Body] Body003  label="Connection001"
  AllowCompound = false
  Group = -> [Sketch007,Pad003,Fillet001,Fillet002,Fillet003]
  Origin = -> Origin017
  Tip = -> Fillet003
FEATURE [App::Part] Part  label="Switch"
  Group = -> [Body001,Body002,Body003]
  Origin = -> Origin014
FEATURE [App::Link] Switch  label="Switch001"
  LinkPlacement = pos=(19.5,24.35,1.67) rot=(0,0,1;0rad)
  LinkedObject = -> Part
  Placement = pos=(19.5,24.35,1.67) rot=(0,0,1;0rad)
FEATURE [App::FeaturePython] Joint012  label="Fixed012"  # Assembly joint (typed FeaturePython)
  Activated = true
  AngleMax = 0
  AngleMin = 0
  Detach1 = false
  Detach2 = false
  Distance = 0
  Distance2 = 0
  EnableAngleMax = false
  EnableAngleMin = false
  EnableLengthMax = false
  EnableLengthMin = false
  JointType = 0 (Fixed)
  LengthMax = 0
  LengthMin = 0
  Offset2 = pos=(0,-45.75,-0.75) rot=(0,0,1;3.14159rad)
  Placement1 = pos=(-32.5,24.5,1.57) rot=(-0.57735,-0.57735,0.57735;4.18879rad)
  Placement2 = pos=(-52,0.15,-0.1) rot=(0.57735,-0.57735,-0.57735;4.18879rad)
  Reference1 = -> Assembly [Board.Edge4,Board.Vertex2]
  Reference2 = -> Assembly [Switch.Body001.Edge29,Switch.Body001.Edge29]
FEATURE [Sketcher::SketchObject] Sketch008
  ArcFitTolerance = 1e-06
  AttachmentSupport = -> [XY_Plane018]
  FullyConstrained = false
  MakeInternals = false
  MapMode = 5
  sketch-geometry (4):
    g0: LineSegment StartX=-16.6992 StartY=16.8811 StartZ=0 EndX=-16.6992 EndY=6.78113 EndZ=0
    g1: LineSegment StartX=-16.6992 StartY=6.78113 StartZ=0 EndX=-6.59923 EndY=6.78113 EndZ=0
    g2: LineSegment StartX=-6.59923 StartY=6.78113 StartZ=0 EndX=-6.59923 EndY=16.8811 EndZ=0
    g3: LineSegment StartX=-6.59923 StartY=16.8811 StartZ=0 EndX=-16.6992 EndY=16.8811 EndZ=0
  constraints (10):
    c: Coincident(g0,g1)
    c: Coincident(g1,g2)
    c: Coincident(g2,g3)
    c: Coincident(g3,g0)
    c: Vertical(g0)
    c: Vertical(g2)
    c: Horizontal(g1)
    c: Horizontal(g3)
    c: DistanceY(g2,g2) = 10.1
    c: DistanceX(g1,g1) = 10.1
FEATURE [PartDesign::Pad] Pad004
  Direction = (0,0,1)
  Length = 4.65
  Length2 = 10
  Profile = -> Sketch008
  ReferenceAxis = -> Sketch008 [N_Axis]
  Refine = true
  Suppressed = false
  Type = 0
FEATURE [PartDesign::Chamfer] Chamfer001
  Angle = 45
  Base = -> Pad004 [Face6,Face5]
  BaseFeature = -> Pad004
  ChamferType = 0
  FlipDirection = false
  Refine = true
  Size = 0.1
  Size2 = 1
  SupportTransform = false
  Suppressed = false
  UseAllEdges = false
FEATURE [PartDesign::Fillet] Fillet004
  Base = -> Chamfer001 [Edge4,Edge16,Edge5,Edge1]
  BaseFeature = -> Chamfer001
  Radius = 0.25
  Refine = true
  SupportTransform = false
  Suppressed = false
  UseAllEdges = false
FEATURE [PartDesign::Body] Body004  label="4R7"
  AllowCompound = false
  Group = -> [Sketch008,Pad004,Chamfer001,Fillet004]
  Origin = -> Origin018
  Tip = -> Fillet004
FEATURE [App::Link] _R7  label="4R008"
  LinkPlacement = pos=(29.1992,-14.2311,1.57) rot=(0,0,1;0rad)
  LinkedObject = -> Body004
  Placement = pos=(29.1992,-14.2311,1.57) rot=(0,0,1;0rad)
FEATURE [App::FeaturePython] Joint013  label="Fixed013"  # Assembly joint (typed FeaturePython)
  Activated = true
  AngleMax = 0
  AngleMin = 0
  Detach1 = false
  Detach2 = false
  Distance = 0
  Distance2 = 0
  EnableAngleMax = false
  EnableAngleMin = false
  EnableLengthMax = false
  EnableLengthMin = false
  JointType = 0 (Fixed)
  LengthMax = 0
  LengthMin = 0
  Offset2 = pos=(0,-10,-26.9) rot=(0,0,1;0rad)
  Placement1 = pos=(-6.69923,11.8311,0) rot=(0.57735,0.57735,0.57735;4.18879rad)
  Placement2 = pos=(22.5,-2.4,1.57) rot=(0.57735,0.57735,0.57735;4.18879rad)
  Reference1 = -> Assembly [_R7.Edge26,_R7.Edge26]
  Reference2 = -> Assembly [Board.Edge16,Board.Vertex12]
FEATURE [Sketcher::SketchObject] Sketch009
  ArcFitTolerance = 1e-06
  AttachmentSupport = -> [XY_Plane019]
  FullyConstrained = false
  MakeInternals = false
  MapMode = 5
  sketch-geometry (8):
    g0: LineSegment StartX=8.01058 StartY=22.151 StartZ=0 EndX=-24.9894 EndY=22.151 EndZ=0
    g1: LineSegment StartX=-24.9894 StartY=22.151 StartZ=0 EndX=-24.9894 EndY=5.65103 EndZ=0
    g2: LineSegment StartX=-24.9894 StartY=5.65103 StartZ=0 EndX=10.0106 EndY=5.65103 EndZ=0
    g3: LineSegment StartX=8.01058 StartY=22.151 StartZ=0 EndX=8.01058 EndY=15.151 EndZ=0
    g4: LineSegment StartX=8.01058 StartY=15.151 StartZ=0 EndX=32.5106 EndY=15.151 EndZ=0
    g5: LineSegment StartX=32.5106 StartY=15.151 StartZ=0 EndX=32.5106 EndY=9.65103 EndZ=0
    g6: LineSegment StartX=32.5106 StartY=9.65103 StartZ=0 EndX=10.0106 EndY=9.65103 EndZ=0
    g7: LineSegment StartX=10.0106 StartY=9.65103 StartZ=0 EndX=10.0106 EndY=5.65103 EndZ=0
  constraints (22):
    c: Horizontal(g0)
    c: Coincident(g1,g0)
    c: Vertical(g1)
    c: Coincident(g2,g1)
    c: Horizontal(g2)
    c: Coincident(g3,g0)
    c: Vertical(g3)
    c: Coincident(g4,g3)
    c: Horizontal(g4)
    c: Coincident(g5,g4)
    c: Vertical(g5)
    c: Coincident(g6,g5)
    c: Horizontal(g6)
    c: Coincident(g7,g6)
    c: Coincident(g7,g2)
    c: Vertical(g7)
    c: DistanceY(g1,g1) = 16.5
    c: DistanceX(g0,g0) = 33
    c: DistanceX(g2,g2) = 35
    c: DistanceY(g5,g5) = 5.5
    c: DistanceY(g3,g3) = 7
    c: DistanceX(g6,g6) = 22.5
FEATURE [PartDesign::Pad] Pad005
  Direction = (0,0,1)
  Length = 0.1
  Length2 = 10
  Profile = -> Sketch009
  ReferenceAxis = -> Sketch009 [N_Axis]
  Refine = true
  Suppressed = false
  Type = 0
FEATURE [PartDesign::Body] Body005  label="Board_Decal001"
  AllowCompound = false
  Group = -> [Sketch009,Pad005]
  Origin = -> Origin019
  Tip = -> Pad005
FEATURE [Sketcher::SketchObject] Sketch010
  ArcFitTolerance = 1e-06
  AttachmentSupport = -> [XY_Plane020]
  FullyConstrained = false
  MakeInternals = false
  MapMode = 5
  sketch-geometry (8):
    g0: LineSegment StartX=-29.0787 StartY=-31.2258 StartZ=0 EndX=25.9213 EndY=-31.2258 EndZ=0
    g1: LineSegment StartX=25.9213 StartY=-31.2258 StartZ=0 EndX=25.9213 EndY=-40.2258 EndZ=0
    g2: LineSegment StartX=25.9213 StartY=-40.2258 StartZ=0 EndX=25.8213 EndY=-40.2258 EndZ=0
    g3: LineSegment StartX=23.9213 StartY=-42.1258 StartZ=0 EndX=23.9213 EndY=-46.2258 EndZ=0
    g4: LineSegment StartX=23.9213 StartY=-46.2258 StartZ=0 EndX=-29.0787 EndY=-46.2258 EndZ=0
    g5: LineSegment StartX=-29.0787 StartY=-46.2258 StartZ=0 EndX=-29.0787 EndY=-31.2258 EndZ=0
    g6: ArcOfCircle CenterX=25.8213 CenterY=-42.1258 CenterZ=0 NormalX=0 NormalY=0 NormalZ=1 AngleXU=0 Radius=1.9 StartAngle=1.5708 EndAngle=3.14159
    g7: GeomPoint [constr] X=23.9213 Y=-40.2258 Z=0
  constraints (20):
    c: Horizontal(g0)
    c: Coincident(g1,g0)
    c: Vertical(g1)
    c: Coincident(g2,g1)
    c: Horizontal(g2)
    c: Vertical(g3)
    c: Coincident(g4,g3)
    c: Horizontal(g4)
    c: Coincident(g5,g4)
    c: Coincident(g5,g0)
    c: Vertical(g5)
    c: DistanceY(g5,g5) = 15
    c: DistanceX(g0,g0) = 55
    c: DistanceX(g4,g4) = 53
    c: DistanceY(g1,g1) = 9
    c: PointOnObject(g7,g2)
    c: PointOnObject(g7,g3)
    c: Tangent(g2,g6) = -1.5708
    c: Tangent(g3,g6) = -1.5708
    c: Radius(g6) = 1.9
FEATURE [PartDesign::Pad] Pad006
  Direction = (0,0,1)
  Length = 0.1
  Length2 = 10
  Profile = -> Sketch010
  ReferenceAxis = -> Sketch010 [N_Axis]
  Refine = true
  Suppressed = false
  Type = 0
FEATURE [PartDesign::Body] Body006  label="Board_Decal002"
  AllowCompound = false
  Group = -> [Sketch010,Pad006]
  Origin = -> Origin020
  Tip = -> Pad006
FEATURE [App::DocumentObjectGroup] Group  label="Parts"
  Group = -> [Body,XH_2_54_2p,DC_JACK_v2,USB_Type_C,B2B_PH_K_S_v3,kf301_v1,Part__Feature,DS1021_black_2x06p_100mil_Type5_rev1_0,Extrude,Part,Body004,Body005,Body006]
FEATURE [App::Link] Board_Decal001  label="Board_Decal003"
  LinkPlacement = pos=(-0.0105772,5.84897,1.57) rot=(0,0,1;0rad)
  LinkedObject = -> Body005
  Placement = pos=(-0.0105772,5.84897,1.57) rot=(0,0,1;0rad)
FEATURE [App::Link] Board_Decal002  label="Board_Decal004"
  LinkPlacement = pos=(3.57869,18.2258,1.57) rot=(0,0,1;0rad)
  LinkedObject = -> Body006
  Placement = pos=(3.57869,18.2258,1.57) rot=(0,0,1;0rad)
FEATURE [App::DocumentObjectGroup] Group001  label="Components"
  Group = -> [Board,DC_JACK_v006,XH_2_54_2p003,DC_JACK_v007,USB_Type_C004,B2B_PH_K_S_v006,B2B_PH_K_S_v007,kf301_v002,__7uF_63V_electr_5_x11mm__P_diameter_2_5mm_Green_Yellow,__7uF_63V_electr_5_x11mm__P_diameter_2_5mm_Green_Yellow001,__7uF_63V_electr_5_x11mm__P_diameter_2_5mm_Green_Yellow002,DS1021_black_2x06p_100mil_Type5_rev1_018,Switch,_R7,Board_Decal001,Board_Decal002]
FEATURE [App::FeaturePython] Joint014  label="Fixed014"  # Assembly joint (typed FeaturePython)
  Activated = true
  AngleMax = 0
  AngleMin = 0
  Detach1 = false
  Detach2 = false
  Distance = 0
  Distance2 = 0
  EnableAngleMax = false
  EnableAngleMin = false
  EnableLengthMax = false
  EnableLengthMin = false
  JointType = 0 (Fixed)
  LengthMax = 0
  LengthMin = 0
  Offset2 = pos=(0,0,8) rot=(0,0,1;0rad)
  Placement1 = pos=(-3.6e-15,28,1.57) rot=(-0.707107,0,0.707107;3.14159rad)
  Placement2 = pos=(0.0105772,22.151,0) rot=(-0.707107,0,0.707107;3.14159rad)
  Reference1 = -> Assembly [Board.Edge22,Board.Edge22]
  Reference2 = -> Assembly [Board_Decal001.Edge3,Board_Decal001.Vertex1]
FEATURE [App::FeaturePython] Joint015  label="Fixed015"  # Assembly joint (typed FeaturePython)
  Activated = true
  AngleMax = 0
  AngleMin = 0
  Detach1 = false
  Detach2 = false
  Distance = 0
  Distance2 = 0
  EnableAngleMax = false
  EnableAngleMin = false
  EnableLengthMax = false
  EnableLengthMin = false
  JointType = 0 (Fixed)
  LengthMax = 0
  LengthMin = 0
  Offset2 = pos=(0,0,1) rot=(0,0,1;3.14159rad)
  Placement1 = pos=(-3.6e-15,-28,1.57) rot=(0.707107,0,0.707107;3.14159rad)
  Placement2 = pos=(-3.57869,-46.2258,0) rot=(0,1,0;4.71239rad)
  Reference1 = -> Assembly [Board.Edge10,Board.Edge10]
  Reference2 = -> Assembly [Board_Decal002.Edge18,Board_Decal002.Edge18]
FEATURE [Assembly::JointGroup] Joints
  Group = -> [GroundedJoint,Joint,Joint001,Joint003,Joint004,Joint005,Joint006,Joint007,Joint008,Joint009,Joint010,Joint011,Joint012,Joint013,Joint014,Joint015]
FEATURE [Assembly::AssemblyObject] Assembly  label="Full Assembly"
  Group = -> [Joints,Joint,Joint001,Joint003,Joint004,Joint005,Joint006,Joint007,Group001,GroundedJoint,Board,DC_JACK_v006,XH_2_54_2p003,DC_JACK_v007,USB_Type_C004,B2B_PH_K_S_v006,B2B_PH_K_S_v007,kf301_v002,__7uF_63V_electr_5_x11mm__P_diameter_2_5mm_Green_Yellow,__7uF_63V_electr_5_x11mm__P_diameter_2_5mm_Green_Yellow001,__7uF_63V_electr_5_x11mm__P_diameter_2_5mm_Green_Yellow002,Joint008,Joint009,Joint010,+10 more]
  Origin = -> Origin
  Type = Assembly
